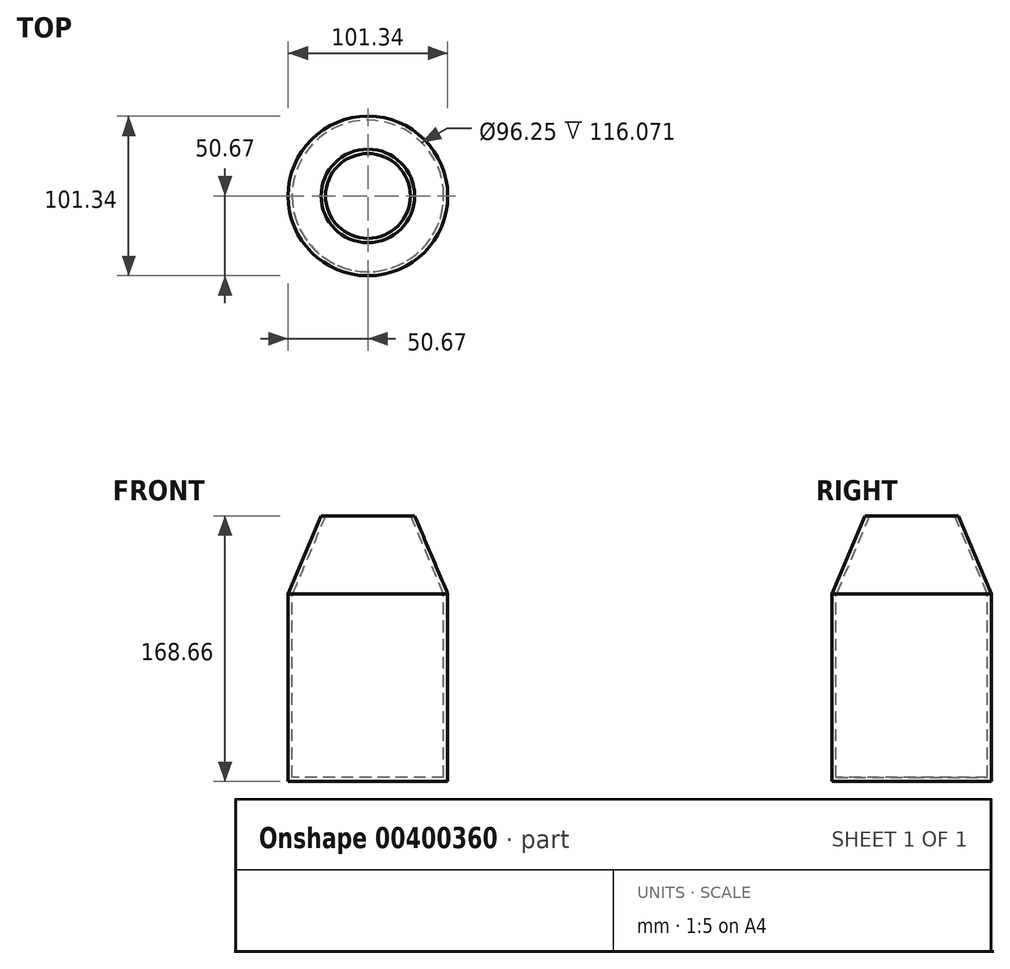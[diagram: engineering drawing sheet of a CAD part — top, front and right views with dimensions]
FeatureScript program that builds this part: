
annotation { "Feature Type Name" : "Feature", "Feature Type Description" : "" }
export const myFeature = defineFeature(function(context is Context, id is Id, definition is map)
    precondition{}
    {
        {
            var Q0;
            Q0=qCreatedBy(makeId("Top.planeOp"),FACE);
            var sketch = newSketch(context, id + "F0", { "sketchPlane" : qUnion([Q0])});
            skCircle(sketch, "E0", {"center": v(0, 0) * mm, "radius": 50.67 * mm});
            skSolve(sketch);
        }
        {
            var Q0;
            Q0=qCreatedBy(makeId("Top.planeOp"),FACE);
            cPlane(context, id + "F1", {"entities" : qUnion([Q0]), "cplaneType" : CPlaneType.OFFSET, "offset" : 49.53 * mm, "width" : 152.4 * mm, "height" : 152.4 * mm});
        }
        {
            var Q0;
            Q0=qCreatedBy(id+"F1.planeOp",FACE);
            var sketch = newSketch(context, id + "F2", { "sketchPlane" : qUnion([Q0])});
            skCircle(sketch, "E1", {"center": v(0, 0) * mm, "radius": 29.71 * mm});
            skSolve(sketch);
        }
        {
            var Q0;
            Q0=makeQuery(id+"F2.imprint","IMPRINT",FACE,{"disambiguationData":[TD([[makeQuery(id+"F2.imprint","IMPRINT",EDGE,{"derivedFrom":sQuery(id+"F2.wireOp",EDGE,"E1")}),1.0]])]});
            var Q1;
            Q1=makeQuery(id+"F0.imprint","IMPRINT",FACE,{"disambiguationData":[TD([[makeQuery(id+"F0.imprint","IMPRINT",EDGE,{"derivedFrom":sQuery(id+"F0.wireOp",EDGE,"E0")}),1.0]])]});
            loft(context, id + "F3", {"sheetProfilesArray" : [{ "sheetProfileEntities" : qUnion([Q0]) }, { "sheetProfileEntities" : qUnion([Q1]) }]});
        }
        {
            var Q0;
            Q0=makeQuery(id+"F3.opLoft","CAP_FACE",FACE,{"disambiguationData":[OSD([makeQuery(id+"F0.imprint","IMPRINT",FACE,{"disambiguationData":[TD([[makeQuery(id+"F0.imprint","IMPRINT",EDGE,{"derivedFrom":sQuery(id+"F0.wireOp",EDGE,"E0")}),1.0]])]})])],"isStart":true});
            extrude(context, id + "F4", {"entities" : qUnion([Q0]), "operationType" : NewBodyOperationType.ADD, "depth" : 119.13 * mm});
        }
        {
            var Q0;
            Q0=makeQuery(id+"F3.opLoft","CAP_FACE",FACE,{"disambiguationData":[OSD([makeQuery(id+"F2.imprint","IMPRINT",FACE,{"disambiguationData":[TD([[makeQuery(id+"F2.imprint","IMPRINT",EDGE,{"derivedFrom":sQuery(id+"F2.wireOp",EDGE,"E1")}),1.0]])]})])],"isStart":true});
            shell(context, id + "F5", {"entities" : qUnion([Q0]), "thickness" : 2.54 * mm});
        }
    });
